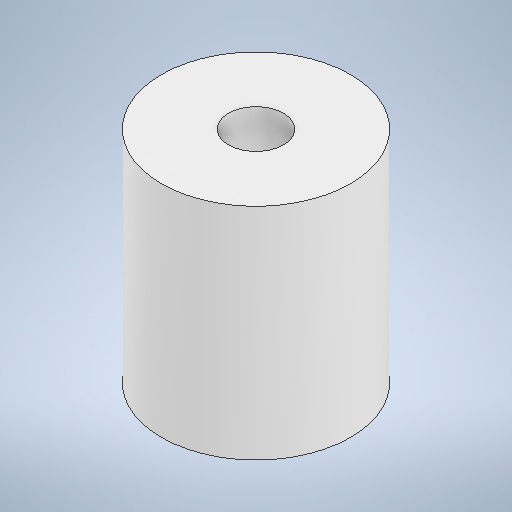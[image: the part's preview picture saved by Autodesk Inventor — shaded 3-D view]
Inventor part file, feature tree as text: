
AUTODESK INVENTOR PART (.ipt)
format: ipt  version: 2025.2 (Build 292293000, 293)  size: 217,600 bytes
history: native  units: mm
features: extrude x2, sketch x2
ambient origin geometry x8: Origin, YZ Plane, XZ Plane, XY Plane, X Axis, Y Axis, Z Axis, Center Point
bodies: Solid1 (feature_tree)
feature tree (4):
  extrude  "Extrusion1"  Depth=8.0mm TaperAngle=0.0deg
  extrude  "Extrusion2"  Depth=8.0mm TaperAngle=0.0deg
  sketch  "Sketch1"  dims[d0=6.88mm d1=8.0mm d2=0.0mm]
  sketch  "Sketch2"  dims[d3=2.0mm d4=8.0mm d5=0.0mm]
